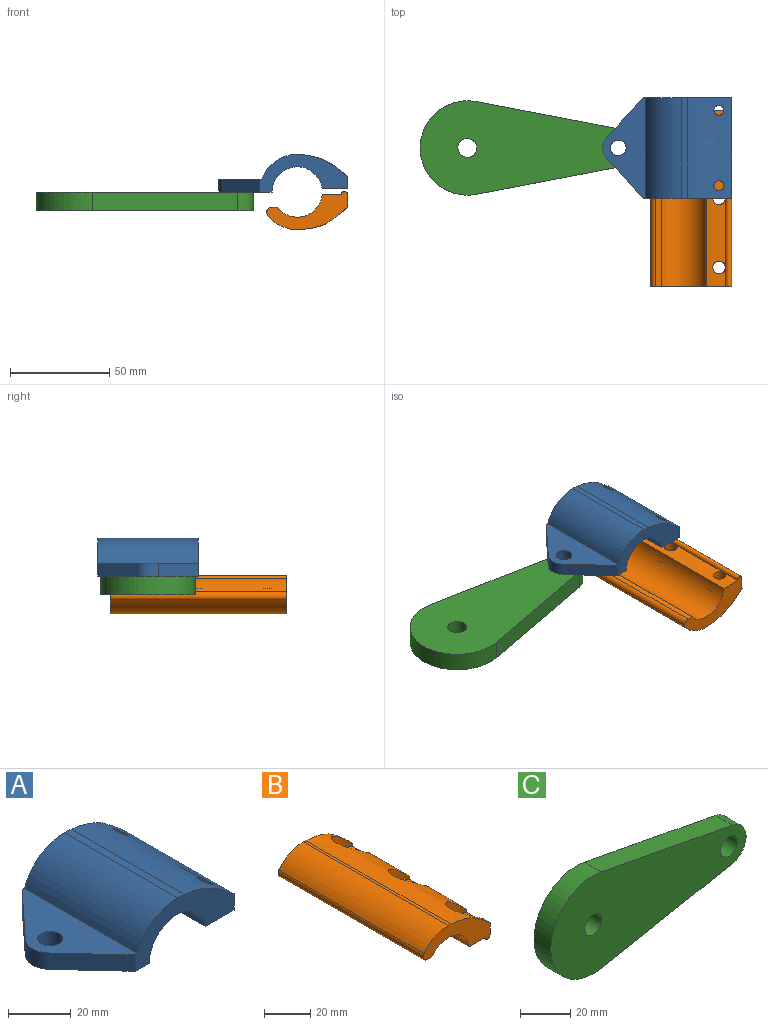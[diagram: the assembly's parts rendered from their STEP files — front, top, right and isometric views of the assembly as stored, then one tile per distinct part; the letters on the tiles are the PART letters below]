
ASSEMBLY  parts=3 mates=1
PART A: 16 faces, bbox 65.1x50.8x19.1 mm
  f0: extruded ~50.8x22.39mm, area 1236.9mm2, adj f2,f3,f8,f9,f14,f15
  f1: plane 50.8x26.99mm, normal (0,0,-1), area 859.2mm2, adj f2,f3,f6,f10,f11,f12,f13
  f2: plane 44.45x19.05mm, normal (0,-1,0), area 403.3mm2, adj f0,f1,f4,f5,f6,f7,f8,f9
  f3: plane 44.45x19.05mm, normal (0,1,0), area 403.3mm2, adj f0,f1,f4,f5,f6,f7,f8,f9
  f4: cylinder r=19.05mm len=50.8mm, axis (0,1,0), area 1191.2mm2, adj f2,f3,f5,f9
  f5: plane 50.8x21.73mm, normal (0,0,1), area 591.9mm2, adj f2,f3,f4,f10,f11,f12,f13
  f6: cylinder r=12.7mm len=50.8mm, axis (0,1,0), area 1946mm2, adj f1,f2,f3,f7
  f7: plane 50.8x12.8mm, normal (0,0,-1), area 609.3mm2, adj f2,f3,f6,f8,f14,f15
  f8: plane 50.8x6.35mm, normal (1,0,0), area 322.6mm2, adj f0,f2,f3,f7
  f9: extruded ~50.8x3.01mm, area 153.5mm2, adj f0,f2,f3,f4
  f10: cylinder r=3.97mm len=7.94mm, axis (0,0,1), area 158.3mm2, adj f1,f5
  f11: plane 20.01x18.52mm, normal (-0.73,0.68,0), area 173.1mm2, adj f1,f3,f5,f12
  f12: cylinder r=7.94mm len=10.79mm, axis (0,0,-1), area 75.3mm2, adj f1,f5,f11,f13
  f13: plane 20.01x18.52mm, normal (-0.73,-0.68,0), area 173.1mm2, adj f1,f2,f5,f12
  f14: cylinder r=2.55mm len=13.01mm, axis (0,0,-1), area 179.6mm2, adj f0,f7
  f15: cylinder r=2.55mm len=13.01mm, axis (0,0,-1), area 179.6mm2, adj f0,f7
PART B: 20 faces, bbox 41x88.9x19.1 mm
  f0: plane 88.9x6.35mm, normal (1,0,0), area 519.2mm2, adj f1,f2,f9,f10,f11,f12,f14,f15
  f1: extruded ~88.9x23.86mm, area 1712.2mm2, adj f0,f3,f9,f10,f12,f15,f18
  f2: cylinder r=1.59mm len=88.9mm, axis (0,1,0), area 443.4mm2, adj f0,f8,f9,f10
  f3: extruded ~88.9x1.54mm, area 137.2mm2, adj f1,f4,f9,f10
  f4: cylinder r=19.05mm len=88.9mm, axis (0,1,0), area 1537.6mm2, adj f3,f5,f9,f10
  f5: cylinder r=2.54mm len=88.9mm, axis (0,1,0), area 504.4mm2, adj f4,f6,f9,f10
  f6: plane 88.9x2.85mm, normal (0,0,-1), area 253.7mm2, adj f5,f7,f9,f10
  f7: cylinder r=12.7mm len=88.9mm, axis (0,1,0), area 2678.9mm2, adj f6,f8,f9,f10
  f8: plane 88.9x9.62mm, normal (0,0,-1), area 760.6mm2, adj f2,f7,f9,f10,f13,f16,f19
  f9: plane 40.95x19.05mm, normal (0,-1,0), area 355.5mm2, adj f0,f1,f2,f3,f4,f5,f6,f7
  f10: plane 40.95x19.05mm, normal (0,1,0), area 355.5mm2, adj f0,f1,f2,f3,f4,f5,f6,f7
  f11: plane 15.88x14.29mm, normal (0,0,1), area 156mm2, adj f0,f12,f13
  f12: cylinder r=7.94mm len=15.88mm, axis (0,0,1), area 301.2mm2, adj f0,f1,f11
  f13: cylinder r=3.17mm len=6.35mm, axis (0,0,1), area 95mm2, adj f8,f11
  f14: plane 15.88x14.29mm, normal (0,0,1), area 156mm2, adj f0,f15,f16
  f15: cylinder r=7.94mm len=15.88mm, axis (0,0,1), area 301.2mm2, adj f0,f1,f14
  f16: cylinder r=3.17mm len=6.35mm, axis (0,0,1), area 95mm2, adj f8,f14
  f17: plane 15.88x14.29mm, normal (0,0,1), area 156mm2, adj f0,f18,f19
  f18: cylinder r=7.94mm len=15.88mm, axis (0,0,1), area 301.2mm2, adj f0,f1,f17
  f19: cylinder r=3.17mm len=6.35mm, axis (0,0,1), area 95mm2, adj f8,f17
PART C: 8 faces, bbox 109.5x9.5x47.6 mm
  f0: cylinder r=9.53mm len=18.71mm, axis (0,1,0), area 250.8mm2, adj f1,f3,f6,f7
  f1: plane 73.52x14.03mm, normal (0.19,0,0.98), area 712.9mm2, adj f0,f2,f6,f7
  f2: cylinder r=23.81mm len=47.63mm, axis (0,1,0), area 798.1mm2, adj f1,f3,f6,f7
  f3: plane 73.52x14.03mm, normal (0.19,0,-0.98), area 712.9mm2, adj f0,f2,f6,f7
  f4: cylinder r=4.76mm len=9.53mm, axis (0,1,0), area 285mm2, adj f6,f7
  f5: cylinder r=4.76mm len=9.53mm, axis (0,1,0), area 285mm2, adj f6,f7
  f6: plane 109.54x47.63mm, normal (0,-1,0), area 3475.8mm2, adj f0,f1,f2,f3,f4,f5
  f7: plane 109.54x47.63mm, normal (0,1,0), area 3475.8mm2, adj f0,f1,f2,f3,f4,f5
PLACE A t=(-128.83,-42.06,-85.5)mm fixed
PLACE B rot(axis=(-1,0,0),180deg) t=(-128.83,-92.86,-85.5)mm
PLACE C rot(axis=(1,0,0),90deg) t=(-160.58,-67.46,-85.5)mm
MATE revolute A.f10 <-> C.f4  axis (0,0,1) through (-160.58,-67.46,-85.5)mm
